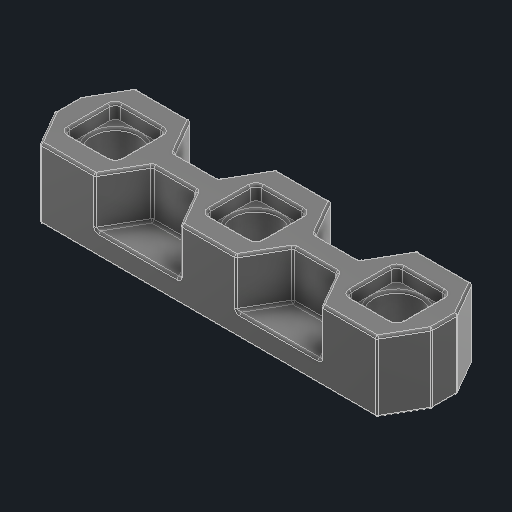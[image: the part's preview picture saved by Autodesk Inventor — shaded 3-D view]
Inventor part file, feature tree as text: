
AUTODESK INVENTOR PART (.ipt)
format: ipt  version: 2025 (Build 290162000, 162)  size: 513,024 bytes
history: native  units: in
note: dims shown in document units (in); Inventor stores cm internally (conversion verified against a paired STEP export)
features: other x3, sketch x1
ambient origin geometry x8: Origin, YZ Plane, XZ Plane, XY Plane, X Axis, Y Axis, Z Axis, Center Point
bodies: Solid1 (feature_tree)
feature tree (4):
  other  "Bearing Flat Low Profile.ipt"
  other  "Solid1::Bearing Flat Low Profile.ipt"
  other  "TaggingFeature1"
  sketch  "Sketch1"  dims[d0=0.3937in]
